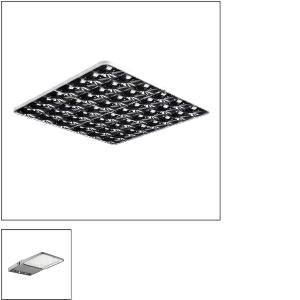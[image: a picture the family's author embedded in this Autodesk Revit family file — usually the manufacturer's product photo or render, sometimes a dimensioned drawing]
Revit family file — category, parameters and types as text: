
# Revit family: siteco_mirrortec_r__indoor___rs05_5nw14091qb_062b
name_source: partatom
category: Lighting Fixtures
units: mm (PartAtom-declared; Revit-internal decimal feet)

## family parameters
Cut with Voids When Loaded = No
Host = Face
Light Source = No
Part Type = Normal
Room Calculation Point = No
Round Connector Dimension = Use Diameter
Shared = No

## types (1)
- 5XA7682G2H2AC (1 x LED, 33820 lm, 305.7 W, 4000K)
    Apparent Load = 306 VA
    CIE Flux Codes = 47 83 98 55 100
    Color Rendering = 70
    Color Temperature = 4000K
    Default Elevation = 1800 mm
    Description = secondary reflector, for Siteco Mirrortec® Indoor, ball-and-socket joint pendant suspension, housing, square, of aluminium, coated, metallic grey (RAL 9006), fresnel reflector 100, of PMMA, aluminized, highly specular, light point resolution, fresnel structure, length: 900 mm, width: 900 mm

Light Distribution: RS05
    Height = 502 mm
    Lamp = 1 x LED
    Lamp Light Flux = 33820 lm
    Lamp Power = 305.7 W
    Lamp count = 1
    Length = 919 mm
    Luminous efficacy = 111 lm/W
    Manufacturer = Siteco
    ModVariant = No
    Model = 5NW14091QB
    Mounting Place = Ceiling
    Mounting Type = Pendant
    Number of Poles = 1
    OnlyDefault = Yes
    Power Factor = 1
    Product Name = Siteco Mirrortec® Indoor | RS05
    Product group = secondary reflector
    ProductGroupID = 908
    Protection Class = Protection class II
    Protection Degree = IP 66
    RLX_Detail_Level = 1
    RLX_Emergency_Light_Flux = 0 lm
    RLX_Emergency_Type = 0
    RLX_Emergency_Type_DB = No
    RlxData = <blob elided: 104725 chars, md5=c2e326ac>
    Socket = socket
    Standby Power = 0 W
    System Light Flux = 33820 lm
    System Power = 306 W
    Type Comments = Floodlight FL 20 midi, floodlight, primary light control with lens, of plastic, primary optical cover: protective disc, of toughened safety glass, transparent, light distribution: RS05, light emission: direct distribution, primary light characteristic: rotationally symmetric, installation type: surface-mounted, LED, High Power LED, rated luminous flux: 38.380lm, luminous efficacy: 126lm/W, light colour: 740, colour temperature: 4000K, control gear: ECG Plus, control: overheat protection, power reduction, digital communication interface, time-dependent luminous flux control, flexible luminous flux parameterisation, electronic power reduction, with terminal, 10-pole, max. 2.5mm², mains connection: 220..240V, AC, 50/60Hz, rated input power: 306W, LED unit, of diecast aluminium, powder-coated, Siteco® metallic grey (DB 702S), corrosivity category C5 mid according to DIN EN ISO 12944, length: 731mm, width: 450mm, height: 76mm, housing frame, of diecast aluminium, powder-coated, Siteco® metallic grey (DB 702S), wall fastening, DALI, protection rating (complete): IP66, insulation class (complete): insulation class II (safety insulation), certification: CE, ENEC, VDE, protection symbol: D, permissible operating ambient temperature: -40..+40°C, permissible operating ambient temperature for outdoor applications: -40..+50°C, standard: DIN EN 12944, packaging unit: 1 piece

individual setting: distance floodlight mirror = 2,5m / reflector tilt = 5°
    Type Image = l_577132_1005944.jpg
    URL = http://relux.com
    VarID = 5xa7682g2h2ac@adj_152969
    Voltage = 0 V
    Weight = 0.00 kg
    Width = 919 mm

## geometry (parser evidence)
native form markers: Blend x4, Sweep x12
no freeform markers — native parametric forms only
